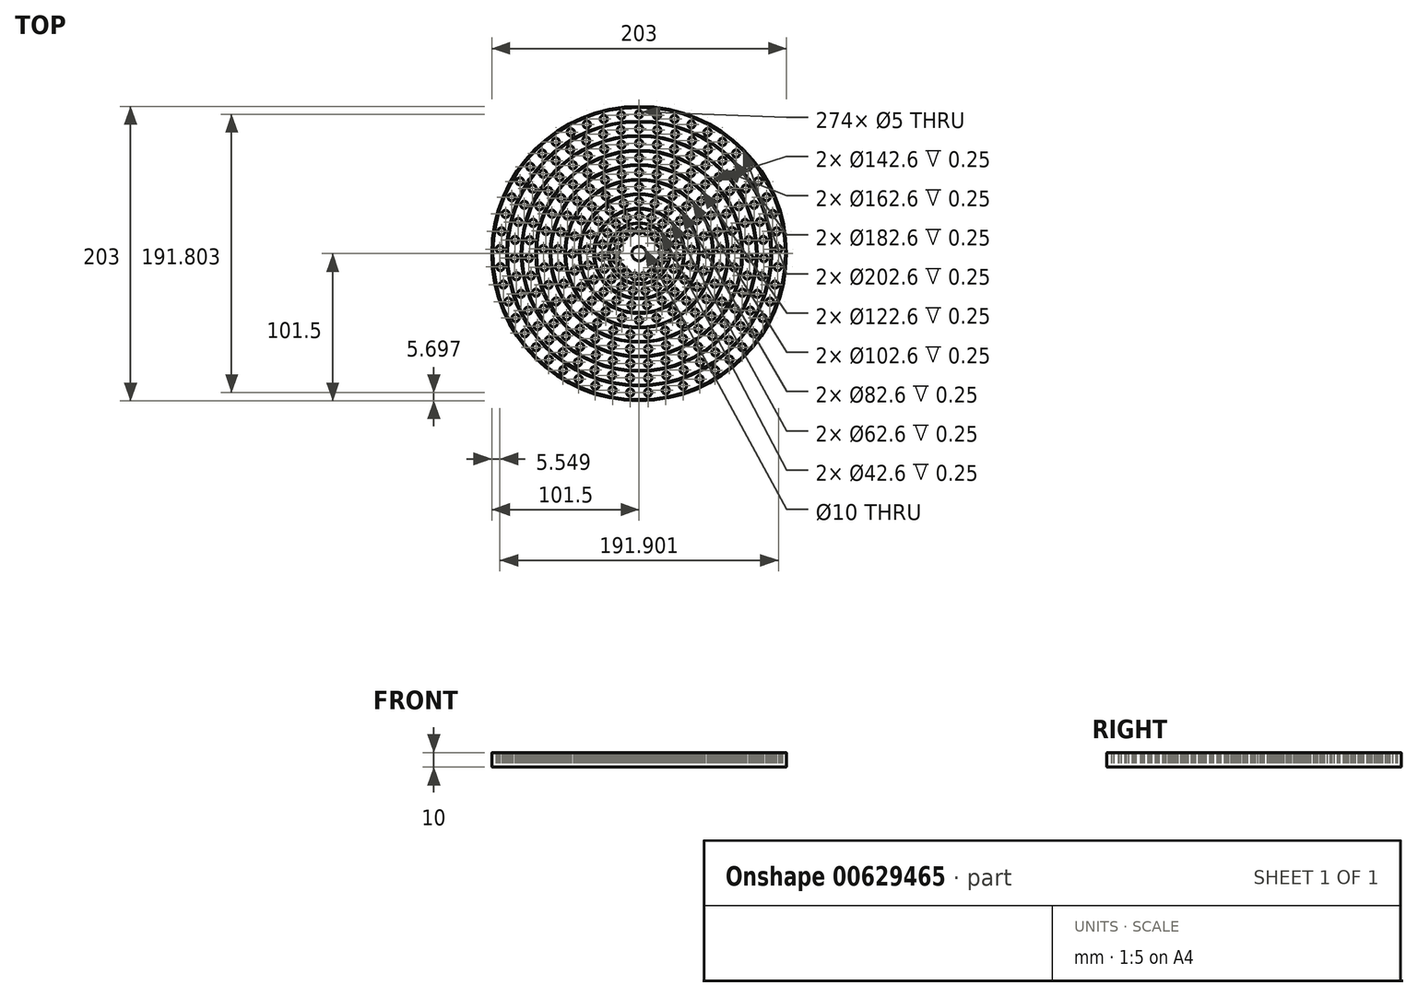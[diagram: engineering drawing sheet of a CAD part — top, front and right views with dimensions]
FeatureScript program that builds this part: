
annotation { "Feature Type Name" : "Feature", "Feature Type Description" : "" }
export const myFeature = defineFeature(function(context is Context, id is Id, definition is map)
    precondition{}
    {
        {
            var Q0;
            Q0=qCreatedBy(makeId("Top.planeOp"),FACE);
            var sketch = newSketch(context, id + "F0", { "sketchPlane" : qUnion([Q0])});
            skCircle(sketch, "E0", {"center": v(0, 0) * mm, "radius": 101.5 * mm});
            skCircle(sketch, "E1", {"center": v(0, 16) * mm, "radius": 2.5 * mm});
            skCircle(sketch, "E2.0.1.0", {"center": v(0, 26) * mm, "radius": 2.5 * mm});
            skCircle(sketch, "E2.0.2.0", {"center": v(0, 36) * mm, "radius": 2.5 * mm});
            skCircle(sketch, "E2.0.3.0", {"center": v(0, 46) * mm, "radius": 2.5 * mm});
            skCircle(sketch, "E2.0.4.0", {"center": v(0, 56) * mm, "radius": 2.5 * mm});
            skCircle(sketch, "E2.0.5.0", {"center": v(0, 66) * mm, "radius": 2.5 * mm});
            skCircle(sketch, "E2.0.6.0", {"center": v(0, 76) * mm, "radius": 2.5 * mm});
            skCircle(sketch, "E2.0.7.0", {"center": v(0, 86) * mm, "radius": 2.5 * mm});
            skCircle(sketch, "E2.0.8.0", {"center": v(0, 96) * mm, "radius": 2.5 * mm});
            skLineSegment(sketch, "E2.direction1", {"start": v(0, 16) * mm, "end": v(25, 16) * mm, "construction": true});
            skLineSegment(sketch, "E2.direction2", {"start": v(0, 16) * mm, "end": v(0, 26) * mm, "construction": true});
            skCircle(sketch, "E3.1.0", {"center": v(-5.78, 14.92) * mm, "radius": 2.5 * mm});
            skCircle(sketch, "E3.2.0", {"center": v(-10.78, 11.82) * mm, "radius": 2.5 * mm});
            skCircle(sketch, "E4.1.3.0", {"center": v(-14.32, 7.13) * mm, "radius": 2.5 * mm});
            skCircle(sketch, "E5.1.0", {"center": v(-8.44, 24.6) * mm, "radius": 2.5 * mm});
            skCircle(sketch, "E5.2.0", {"center": v(-15.97, 20.52) * mm, "radius": 2.5 * mm});
            skCircle(sketch, "E5.3.0", {"center": v(-21.77, 14.22) * mm, "radius": 2.5 * mm});
            skCircle(sketch, "E5.4.0", {"center": v(-25.2, 6.38) * mm, "radius": 2.5 * mm});
            skCircle(sketch, "E5.5.0", {"center": v(-25.91, -2.15) * mm, "radius": 2.5 * mm});
            skCircle(sketch, "E6.1.0", {"center": v(-10.61, 34.4) * mm, "radius": 2.5 * mm});
            skCircle(sketch, "E6.2.0", {"center": v(-20.28, 29.74) * mm, "radius": 2.5 * mm});
            skCircle(sketch, "E6.3.0", {"center": v(-28.15, 22.45) * mm, "radius": 2.5 * mm});
            skCircle(sketch, "E6.4.0", {"center": v(-33.51, 13.15) * mm, "radius": 2.5 * mm});
            skCircle(sketch, "E6.5.0", {"center": v(-35.9, 2.7) * mm, "radius": 2.5 * mm});
            skCircle(sketch, "E6.6.0", {"center": v(-35.1, -8.01) * mm, "radius": 2.5 * mm});
            skCircle(sketch, "E6.7.0", {"center": v(-31.18, -18) * mm, "radius": 2.5 * mm});
            skCircle(sketch, "E7.1.0", {"center": v(-11.9, 44.43) * mm, "radius": 2.5 * mm});
            skCircle(sketch, "E7.2.0", {"center": v(-23, 39.84) * mm, "radius": 2.5 * mm});
            skCircle(sketch, "E7.3.0", {"center": v(-32.53, 32.53) * mm, "radius": 2.5 * mm});
            skCircle(sketch, "E7.4.0", {"center": v(-39.84, 23) * mm, "radius": 2.5 * mm});
            skCircle(sketch, "E7.5.0", {"center": v(-44.43, 11.9) * mm, "radius": 2.5 * mm});
            skCircle(sketch, "E7.6.0", {"center": v(-46, 0) * mm, "radius": 2.5 * mm});
            skCircle(sketch, "E7.7.0", {"center": v(-44.43, -11.9) * mm, "radius": 2.5 * mm});
            skCircle(sketch, "E7.8.0", {"center": v(-39.84, -23) * mm, "radius": 2.5 * mm});
            skCircle(sketch, "E7.9.0", {"center": v(-32.53, -32.53) * mm, "radius": 2.5 * mm});
            skCircle(sketch, "E8.1.0", {"center": v(-12.5, 64.8) * mm, "radius": 2.5 * mm});
            skCircle(sketch, "E8.2.0", {"center": v(-24.53, 61.27) * mm, "radius": 2.5 * mm});
            skCircle(sketch, "E8.3.0", {"center": v(-35.68, 55.52) * mm, "radius": 2.5 * mm});
            skCircle(sketch, "E8.4.0", {"center": v(-45.55, 47.77) * mm, "radius": 2.5 * mm});
            skCircle(sketch, "E8.5.0", {"center": v(-53.76, 38.28) * mm, "radius": 2.5 * mm});
            skCircle(sketch, "E8.6.0", {"center": v(-60.04, 27.42) * mm, "radius": 2.5 * mm});
            skCircle(sketch, "E8.7.0", {"center": v(-64.14, 15.56) * mm, "radius": 2.5 * mm});
            skCircle(sketch, "E8.8.0", {"center": v(-65.93, 3.14) * mm, "radius": 2.5 * mm});
            skCircle(sketch, "E8.9.0", {"center": v(-65.33, -9.4) * mm, "radius": 2.5 * mm});
            skCircle(sketch, "E8.10.0", {"center": v(-62.37, -21.59) * mm, "radius": 2.5 * mm});
            skCircle(sketch, "E8.11.0", {"center": v(-57.16, -33) * mm, "radius": 2.5 * mm});
            skCircle(sketch, "E9.1.0", {"center": v(-12.2, 75.02) * mm, "radius": 2.5 * mm});
            skCircle(sketch, "E9.2.0", {"center": v(-24.07, 72.09) * mm, "radius": 2.5 * mm});
            skCircle(sketch, "E9.3.0", {"center": v(-35.32, 67.3) * mm, "radius": 2.5 * mm});
            skCircle(sketch, "E9.4.0", {"center": v(-45.66, 60.76) * mm, "radius": 2.5 * mm});
            skCircle(sketch, "E9.5.0", {"center": v(-54.81, 52.65) * mm, "radius": 2.5 * mm});
            skCircle(sketch, "E9.6.0", {"center": v(-62.55, 43.17) * mm, "radius": 2.5 * mm});
            skCircle(sketch, "E9.7.0", {"center": v(-68.66, 32.58) * mm, "radius": 2.5 * mm});
            skCircle(sketch, "E9.8.0", {"center": v(-73, 21.14) * mm, "radius": 2.5 * mm});
            skCircle(sketch, "E9.9.0", {"center": v(-75.45, 9.16) * mm, "radius": 2.5 * mm});
            skCircle(sketch, "E9.10.0", {"center": v(-75.94, -3.06) * mm, "radius": 2.5 * mm});
            skCircle(sketch, "E9.11.0", {"center": v(-74.46, -15.2) * mm, "radius": 2.5 * mm});
            skCircle(sketch, "E9.12.0", {"center": v(-71.06, -26.95) * mm, "radius": 2.5 * mm});
            skCircle(sketch, "E9.13.0", {"center": v(-65.82, -38) * mm, "radius": 2.5 * mm});
            skCircle(sketch, "E9.14.0", {"center": v(-58.87, -48.07) * mm, "radius": 2.5 * mm});
            skCircle(sketch, "E9.15.0", {"center": v(-50.4, -56.89) * mm, "radius": 2.5 * mm});
            skCircle(sketch, "E10.1.0", {"center": v(-12.28, 95.21) * mm, "radius": 2.5 * mm});
            skCircle(sketch, "E10.2.0", {"center": v(-24.35, 92.86) * mm, "radius": 2.5 * mm});
            skCircle(sketch, "E10.3.0", {"center": v(-36.03, 88.98) * mm, "radius": 2.5 * mm});
            skCircle(sketch, "E10.4.0", {"center": v(-47.1, 83.65) * mm, "radius": 2.5 * mm});
            skCircle(sketch, "E10.5.0", {"center": v(-57.42, 76.94) * mm, "radius": 2.5 * mm});
            skCircle(sketch, "E10.6.0", {"center": v(-66.79, 68.96) * mm, "radius": 2.5 * mm});
            skCircle(sketch, "E10.7.0", {"center": v(-75.06, 59.86) * mm, "radius": 2.5 * mm});
            skCircle(sketch, "E10.8.0", {"center": v(-82.1, 49.77) * mm, "radius": 2.5 * mm});
            skCircle(sketch, "E10.9.0", {"center": v(-87.78, 38.86) * mm, "radius": 2.5 * mm});
            skCircle(sketch, "E10.10.0", {"center": v(-92.03, 27.31) * mm, "radius": 2.5 * mm});
            skCircle(sketch, "E10.11.0", {"center": v(-94.77, 15.32) * mm, "radius": 2.5 * mm});
            skCircle(sketch, "E10.12.0", {"center": v(-95.95, 3.08) * mm, "radius": 2.5 * mm});
            skCircle(sketch, "E10.13.0", {"center": v(-95.56, -9.22) * mm, "radius": 2.5 * mm});
            skCircle(sketch, "E10.14.0", {"center": v(-93.6, -21.36) * mm, "radius": 2.5 * mm});
            skCircle(sketch, "E10.15.0", {"center": v(-90.1, -33.16) * mm, "radius": 2.5 * mm});
            skCircle(sketch, "E10.16.0", {"center": v(-85.11, -44.4) * mm, "radius": 2.5 * mm});
            skCircle(sketch, "E10.17.0", {"center": v(-78.74, -54.92) * mm, "radius": 2.5 * mm});
            skCircle(sketch, "E11.1.4.0", {"center": v(-15.93, 1.48) * mm, "radius": 2.5 * mm});
            skCircle(sketch, "E11.1.5.0", {"center": v(-15.39, -4.38) * mm, "radius": 2.5 * mm});
            skCircle(sketch, "E11.1.6.0", {"center": v(-12.77, -9.64) * mm, "radius": 2.5 * mm});
            skCircle(sketch, "E11.1.7.0", {"center": v(-8.42, -13.6) * mm, "radius": 2.5 * mm});
            skCircle(sketch, "E11.1.8.0", {"center": v(-2.94, -15.73) * mm, "radius": 2.5 * mm});
            skCircle(sketch, "E11.1.9.0", {"center": v(2.94, -15.73) * mm, "radius": 2.5 * mm});
            skCircle(sketch, "E11.1.10.0", {"center": v(8.42, -13.6) * mm, "radius": 2.5 * mm});
            skCircle(sketch, "E11.1.11.0", {"center": v(12.77, -9.64) * mm, "radius": 2.5 * mm});
            skCircle(sketch, "E11.1.12.0", {"center": v(15.39, -4.38) * mm, "radius": 2.5 * mm});
            skCircle(sketch, "E11.1.13.0", {"center": v(15.93, 1.48) * mm, "radius": 2.5 * mm});
            skCircle(sketch, "E11.1.14.0", {"center": v(14.32, 7.13) * mm, "radius": 2.5 * mm});
            skCircle(sketch, "E11.1.15.0", {"center": v(10.78, 11.82) * mm, "radius": 2.5 * mm});
            skCircle(sketch, "E11.1.16.0", {"center": v(5.78, 14.92) * mm, "radius": 2.5 * mm});
            skCircle(sketch, "E12.1.6.0", {"center": v(-23.81, -10.44) * mm, "radius": 2.5 * mm});
            skCircle(sketch, "E12.1.7.0", {"center": v(-19.13, -17.6) * mm, "radius": 2.5 * mm});
            skCircle(sketch, "E12.1.8.0", {"center": v(-12.37, -22.87) * mm, "radius": 2.5 * mm});
            skCircle(sketch, "E12.1.9.0", {"center": v(-4.28, -25.65) * mm, "radius": 2.5 * mm});
            skCircle(sketch, "E12.1.10.0", {"center": v(4.28, -25.65) * mm, "radius": 2.5 * mm});
            skCircle(sketch, "E12.1.11.0", {"center": v(12.37, -22.87) * mm, "radius": 2.5 * mm});
            skCircle(sketch, "E12.1.12.0", {"center": v(19.13, -17.6) * mm, "radius": 2.5 * mm});
            skCircle(sketch, "E12.1.13.0", {"center": v(23.81, -10.44) * mm, "radius": 2.5 * mm});
            skCircle(sketch, "E12.1.14.0", {"center": v(25.91, -2.15) * mm, "radius": 2.5 * mm});
            skCircle(sketch, "E12.1.15.0", {"center": v(25.2, 6.38) * mm, "radius": 2.5 * mm});
            skCircle(sketch, "E12.1.16.0", {"center": v(21.77, 14.22) * mm, "radius": 2.5 * mm});
            skCircle(sketch, "E12.1.17.0", {"center": v(15.97, 20.52) * mm, "radius": 2.5 * mm});
            skCircle(sketch, "E12.1.18.0", {"center": v(8.44, 24.6) * mm, "radius": 2.5 * mm});
            skCircle(sketch, "E13.1.8.0", {"center": v(-24.49, -26.39) * mm, "radius": 2.5 * mm});
            skCircle(sketch, "E13.1.9.0", {"center": v(-15.62, -32.43) * mm, "radius": 2.5 * mm});
            skCircle(sketch, "E13.1.10.0", {"center": v(-5.37, -35.6) * mm, "radius": 2.5 * mm});
            skCircle(sketch, "E13.1.11.0", {"center": v(5.37, -35.6) * mm, "radius": 2.5 * mm});
            skCircle(sketch, "E13.1.12.0", {"center": v(15.62, -32.43) * mm, "radius": 2.5 * mm});
            skCircle(sketch, "E13.1.13.0", {"center": v(24.49, -26.39) * mm, "radius": 2.5 * mm});
            skCircle(sketch, "E13.1.14.0", {"center": v(31.18, -18) * mm, "radius": 2.5 * mm});
            skCircle(sketch, "E13.1.15.0", {"center": v(35.1, -8.01) * mm, "radius": 2.5 * mm});
            skCircle(sketch, "E13.1.16.0", {"center": v(35.9, 2.7) * mm, "radius": 2.5 * mm});
            skCircle(sketch, "E13.1.17.0", {"center": v(33.51, 13.15) * mm, "radius": 2.5 * mm});
            skCircle(sketch, "E13.1.18.0", {"center": v(28.15, 22.45) * mm, "radius": 2.5 * mm});
            skCircle(sketch, "E13.1.19.0", {"center": v(20.28, 29.74) * mm, "radius": 2.5 * mm});
            skCircle(sketch, "E13.1.20.0", {"center": v(10.61, 34.4) * mm, "radius": 2.5 * mm});
            skCircle(sketch, "E14.1.10.0", {"center": v(-23, -39.84) * mm, "radius": 2.5 * mm});
            skCircle(sketch, "E14.1.11.0", {"center": v(-11.9, -44.43) * mm, "radius": 2.5 * mm});
            skCircle(sketch, "E14.1.12.0", {"center": v(0, -46) * mm, "radius": 2.5 * mm});
            skCircle(sketch, "E14.1.13.0", {"center": v(11.9, -44.43) * mm, "radius": 2.5 * mm});
            skCircle(sketch, "E14.1.14.0", {"center": v(23, -39.84) * mm, "radius": 2.5 * mm});
            skCircle(sketch, "E14.1.15.0", {"center": v(32.53, -32.53) * mm, "radius": 2.5 * mm});
            skCircle(sketch, "E14.1.16.0", {"center": v(39.84, -23) * mm, "radius": 2.5 * mm});
            skCircle(sketch, "E14.1.17.0", {"center": v(44.43, -11.9) * mm, "radius": 2.5 * mm});
            skCircle(sketch, "E14.1.18.0", {"center": v(46, 0) * mm, "radius": 2.5 * mm});
            skCircle(sketch, "E14.1.19.0", {"center": v(44.43, 11.9) * mm, "radius": 2.5 * mm});
            skCircle(sketch, "E14.1.20.0", {"center": v(39.84, 23) * mm, "radius": 2.5 * mm});
            skCircle(sketch, "E14.1.21.0", {"center": v(32.53, 32.53) * mm, "radius": 2.5 * mm});
            skCircle(sketch, "E14.1.22.0", {"center": v(23, 39.84) * mm, "radius": 2.5 * mm});
            skCircle(sketch, "E14.1.23.0", {"center": v(11.9, 44.43) * mm, "radius": 2.5 * mm});
            skCircle(sketch, "E15.1.0", {"center": v(-12.04, 54.7) * mm, "radius": 2.5 * mm});
            skCircle(sketch, "E15.2.0", {"center": v(-23.51, 50.82) * mm, "radius": 2.5 * mm});
            skCircle(sketch, "E16.1.3.0", {"center": v(-33.89, 44.58) * mm, "radius": 2.5 * mm});
            skCircle(sketch, "E16.1.4.0", {"center": v(-42.68, 36.25) * mm, "radius": 2.5 * mm});
            skCircle(sketch, "E16.1.5.0", {"center": v(-49.48, 26.23) * mm, "radius": 2.5 * mm});
            skCircle(sketch, "E16.1.6.0", {"center": v(-53.96, 14.98) * mm, "radius": 2.5 * mm});
            skCircle(sketch, "E16.1.7.0", {"center": v(-55.92, 3.03) * mm, "radius": 2.5 * mm});
            skCircle(sketch, "E16.1.8.0", {"center": v(-55.26, -9.06) * mm, "radius": 2.5 * mm});
            skCircle(sketch, "E16.1.9.0", {"center": v(-52.02, -20.73) * mm, "radius": 2.5 * mm});
            skCircle(sketch, "E16.1.10.0", {"center": v(-46.35, -31.43) * mm, "radius": 2.5 * mm});
            skCircle(sketch, "E16.1.11.0", {"center": v(-38.51, -40.66) * mm, "radius": 2.5 * mm});
            skCircle(sketch, "E16.1.12.0", {"center": v(-28.87, -47.98) * mm, "radius": 2.5 * mm});
            skCircle(sketch, "E16.1.13.0", {"center": v(-17.88, -53.07) * mm, "radius": 2.5 * mm});
            skCircle(sketch, "E16.1.14.0", {"center": v(-6.05, -55.67) * mm, "radius": 2.5 * mm});
            skCircle(sketch, "E16.1.15.0", {"center": v(6.05, -55.67) * mm, "radius": 2.5 * mm});
            skCircle(sketch, "E16.1.16.0", {"center": v(17.88, -53.07) * mm, "radius": 2.5 * mm});
            skCircle(sketch, "E16.1.17.0", {"center": v(28.87, -47.98) * mm, "radius": 2.5 * mm});
            skCircle(sketch, "E16.1.18.0", {"center": v(38.51, -40.66) * mm, "radius": 2.5 * mm});
            skCircle(sketch, "E16.1.19.0", {"center": v(46.35, -31.43) * mm, "radius": 2.5 * mm});
            skCircle(sketch, "E16.1.20.0", {"center": v(52.02, -20.73) * mm, "radius": 2.5 * mm});
            skCircle(sketch, "E16.1.21.0", {"center": v(55.26, -9.06) * mm, "radius": 2.5 * mm});
            skCircle(sketch, "E16.1.22.0", {"center": v(55.92, 3.03) * mm, "radius": 2.5 * mm});
            skCircle(sketch, "E16.1.23.0", {"center": v(53.96, 14.98) * mm, "radius": 2.5 * mm});
            skCircle(sketch, "E16.1.24.0", {"center": v(49.48, 26.23) * mm, "radius": 2.5 * mm});
            skCircle(sketch, "E16.1.25.0", {"center": v(42.68, 36.25) * mm, "radius": 2.5 * mm});
            skCircle(sketch, "E16.1.26.0", {"center": v(33.89, 44.58) * mm, "radius": 2.5 * mm});
            skCircle(sketch, "E16.1.27.0", {"center": v(23.51, 50.82) * mm, "radius": 2.5 * mm});
            skCircle(sketch, "E16.1.28.0", {"center": v(12.04, 54.7) * mm, "radius": 2.5 * mm});
            skCircle(sketch, "E17.1.12.0", {"center": v(-49.88, -43.22) * mm, "radius": 2.5 * mm});
            skCircle(sketch, "E17.1.13.0", {"center": v(-40.8, -51.88) * mm, "radius": 2.5 * mm});
            skCircle(sketch, "E17.1.14.0", {"center": v(-30.24, -58.66) * mm, "radius": 2.5 * mm});
            skCircle(sketch, "E17.1.15.0", {"center": v(-18.6, -63.33) * mm, "radius": 2.5 * mm});
            skCircle(sketch, "E17.1.16.0", {"center": v(-6.27, -65.7) * mm, "radius": 2.5 * mm});
            skCircle(sketch, "E17.1.17.0", {"center": v(6.27, -65.7) * mm, "radius": 2.5 * mm});
            skCircle(sketch, "E17.1.18.0", {"center": v(18.6, -63.33) * mm, "radius": 2.5 * mm});
            skCircle(sketch, "E17.1.19.0", {"center": v(30.24, -58.66) * mm, "radius": 2.5 * mm});
            skCircle(sketch, "E17.1.20.0", {"center": v(40.8, -51.88) * mm, "radius": 2.5 * mm});
            skCircle(sketch, "E17.1.21.0", {"center": v(49.88, -43.22) * mm, "radius": 2.5 * mm});
            skCircle(sketch, "E17.1.22.0", {"center": v(57.16, -33) * mm, "radius": 2.5 * mm});
            skCircle(sketch, "E17.1.23.0", {"center": v(62.37, -21.59) * mm, "radius": 2.5 * mm});
            skCircle(sketch, "E17.1.24.0", {"center": v(65.33, -9.4) * mm, "radius": 2.5 * mm});
            skCircle(sketch, "E17.1.25.0", {"center": v(65.93, 3.14) * mm, "radius": 2.5 * mm});
            skCircle(sketch, "E17.1.26.0", {"center": v(64.14, 15.56) * mm, "radius": 2.5 * mm});
            skCircle(sketch, "E17.1.27.0", {"center": v(60.04, 27.42) * mm, "radius": 2.5 * mm});
            skCircle(sketch, "E17.1.28.0", {"center": v(53.76, 38.28) * mm, "radius": 2.5 * mm});
            skCircle(sketch, "E18.1.29.0", {"center": v(45.55, 47.77) * mm, "radius": 2.5 * mm});
            skCircle(sketch, "E18.1.30.0", {"center": v(35.68, 55.52) * mm, "radius": 2.5 * mm});
            skCircle(sketch, "E18.1.31.0", {"center": v(24.53, 61.27) * mm, "radius": 2.5 * mm});
            skCircle(sketch, "E18.1.32.0", {"center": v(12.5, 64.8) * mm, "radius": 2.5 * mm});
            skCircle(sketch, "E19.1.16.0", {"center": v(-40.62, -64.23) * mm, "radius": 2.5 * mm});
            skCircle(sketch, "E19.1.17.0", {"center": v(-29.79, -69.92) * mm, "radius": 2.5 * mm});
            skCircle(sketch, "E19.1.18.0", {"center": v(-18.19, -73.8) * mm, "radius": 2.5 * mm});
            skCircle(sketch, "E19.1.19.0", {"center": v(-6.12, -75.75) * mm, "radius": 2.5 * mm});
            skCircle(sketch, "E19.1.20.0", {"center": v(6.12, -75.75) * mm, "radius": 2.5 * mm});
            skCircle(sketch, "E19.1.21.0", {"center": v(18.19, -73.8) * mm, "radius": 2.5 * mm});
            skCircle(sketch, "E19.1.22.0", {"center": v(29.79, -69.92) * mm, "radius": 2.5 * mm});
            skCircle(sketch, "E19.1.23.0", {"center": v(40.62, -64.23) * mm, "radius": 2.5 * mm});
            skCircle(sketch, "E19.1.24.0", {"center": v(50.4, -56.89) * mm, "radius": 2.5 * mm});
            skCircle(sketch, "E19.1.25.0", {"center": v(58.87, -48.07) * mm, "radius": 2.5 * mm});
            skCircle(sketch, "E19.1.26.0", {"center": v(65.82, -38) * mm, "radius": 2.5 * mm});
            skCircle(sketch, "E19.1.27.0", {"center": v(71.06, -26.95) * mm, "radius": 2.5 * mm});
            skCircle(sketch, "E19.1.28.0", {"center": v(74.46, -15.2) * mm, "radius": 2.5 * mm});
            skCircle(sketch, "E19.1.29.0", {"center": v(75.94, -3.06) * mm, "radius": 2.5 * mm});
            skCircle(sketch, "E19.1.30.0", {"center": v(75.45, 9.16) * mm, "radius": 2.5 * mm});
            skCircle(sketch, "E19.1.31.0", {"center": v(73, 21.14) * mm, "radius": 2.5 * mm});
            skCircle(sketch, "E19.1.32.0", {"center": v(68.66, 32.58) * mm, "radius": 2.5 * mm});
            skCircle(sketch, "E19.1.33.0", {"center": v(62.55, 43.17) * mm, "radius": 2.5 * mm});
            skCircle(sketch, "E19.1.34.0", {"center": v(54.81, 52.65) * mm, "radius": 2.5 * mm});
            skCircle(sketch, "E19.1.35.0", {"center": v(45.66, 60.76) * mm, "radius": 2.5 * mm});
            skCircle(sketch, "E19.1.36.0", {"center": v(35.32, 67.3) * mm, "radius": 2.5 * mm});
            skCircle(sketch, "E19.1.37.0", {"center": v(24.07, 72.09) * mm, "radius": 2.5 * mm});
            skCircle(sketch, "E19.1.38.0", {"center": v(12.2, 75.02) * mm, "radius": 2.5 * mm});
            skCircle(sketch, "E20.1.18.0", {"center": v(-71.07, -64.54) * mm, "radius": 2.5 * mm});
            skCircle(sketch, "E20.1.19.0", {"center": v(-62.23, -73.1) * mm, "radius": 2.5 * mm});
            skCircle(sketch, "E20.1.20.0", {"center": v(-52.37, -80.46) * mm, "radius": 2.5 * mm});
            skCircle(sketch, "E20.1.21.0", {"center": v(-41.65, -86.5) * mm, "radius": 2.5 * mm});
            skCircle(sketch, "E20.1.22.0", {"center": v(-30.25, -91.1) * mm, "radius": 2.5 * mm});
            skCircle(sketch, "E20.1.23.0", {"center": v(-18.35, -94.23) * mm, "radius": 2.5 * mm});
            skCircle(sketch, "E20.1.24.0", {"center": v(-6.15, -95.8) * mm, "radius": 2.5 * mm});
            skCircle(sketch, "E20.1.25.0", {"center": v(6.15, -95.8) * mm, "radius": 2.5 * mm});
            skCircle(sketch, "E20.1.26.0", {"center": v(18.35, -94.23) * mm, "radius": 2.5 * mm});
            skCircle(sketch, "E20.1.27.0", {"center": v(30.25, -91.1) * mm, "radius": 2.5 * mm});
            skCircle(sketch, "E20.1.28.0", {"center": v(41.65, -86.5) * mm, "radius": 2.5 * mm});
            skCircle(sketch, "E20.1.29.0", {"center": v(52.37, -80.46) * mm, "radius": 2.5 * mm});
            skCircle(sketch, "E20.1.30.0", {"center": v(62.23, -73.1) * mm, "radius": 2.5 * mm});
            skCircle(sketch, "E20.1.31.0", {"center": v(71.07, -64.54) * mm, "radius": 2.5 * mm});
            skCircle(sketch, "E20.1.32.0", {"center": v(78.74, -54.92) * mm, "radius": 2.5 * mm});
            skCircle(sketch, "E20.1.33.0", {"center": v(85.11, -44.4) * mm, "radius": 2.5 * mm});
            skCircle(sketch, "E20.1.34.0", {"center": v(90.1, -33.16) * mm, "radius": 2.5 * mm});
            skCircle(sketch, "E20.1.35.0", {"center": v(93.6, -21.36) * mm, "radius": 2.5 * mm});
            skCircle(sketch, "E20.1.36.0", {"center": v(95.56, -9.22) * mm, "radius": 2.5 * mm});
            skCircle(sketch, "E20.1.37.0", {"center": v(95.95, 3.08) * mm, "radius": 2.5 * mm});
            skCircle(sketch, "E20.1.38.0", {"center": v(94.77, 15.32) * mm, "radius": 2.5 * mm});
            skCircle(sketch, "E20.1.39.0", {"center": v(92.03, 27.31) * mm, "radius": 2.5 * mm});
            skCircle(sketch, "E20.1.40.0", {"center": v(87.78, 38.86) * mm, "radius": 2.5 * mm});
            skCircle(sketch, "E20.1.41.0", {"center": v(82.1, 49.77) * mm, "radius": 2.5 * mm});
            skCircle(sketch, "E20.1.42.0", {"center": v(75.06, 59.86) * mm, "radius": 2.5 * mm});
            skCircle(sketch, "E21.1.0", {"center": v(-12.52, 85.08) * mm, "radius": 2.5 * mm});
            skCircle(sketch, "E21.2.0", {"center": v(-24.78, 82.35) * mm, "radius": 2.5 * mm});
            skCircle(sketch, "E22.1.3.0", {"center": v(-36.5, 77.87) * mm, "radius": 2.5 * mm});
            skCircle(sketch, "E22.1.4.0", {"center": v(-47.45, 71.72) * mm, "radius": 2.5 * mm});
            skCircle(sketch, "E22.1.5.0", {"center": v(-57.39, 64.05) * mm, "radius": 2.5 * mm});
            skCircle(sketch, "E22.1.6.0", {"center": v(-66.1, 55.01) * mm, "radius": 2.5 * mm});
            skCircle(sketch, "E22.1.7.0", {"center": v(-73.4, 44.8) * mm, "radius": 2.5 * mm});
            skCircle(sketch, "E22.1.8.0", {"center": v(-79.15, 33.64) * mm, "radius": 2.5 * mm});
            skCircle(sketch, "E22.1.9.0", {"center": v(-83.2, 21.75) * mm, "radius": 2.5 * mm});
            skCircle(sketch, "E22.1.10.0", {"center": v(-85.48, 9.4) * mm, "radius": 2.5 * mm});
            skCircle(sketch, "E22.1.11.0", {"center": v(-85.94, -3.14) * mm, "radius": 2.5 * mm});
            skCircle(sketch, "E22.1.12.0", {"center": v(-84.57, -15.62) * mm, "radius": 2.5 * mm});
            skCircle(sketch, "E22.1.13.0", {"center": v(-81.4, -27.77) * mm, "radius": 2.5 * mm});
            skCircle(sketch, "E22.1.14.0", {"center": v(-76.48, -39.32) * mm, "radius": 2.5 * mm});
            skCircle(sketch, "E22.1.15.0", {"center": v(-69.94, -50.04) * mm, "radius": 2.5 * mm});
            skCircle(sketch, "E22.1.16.0", {"center": v(-61.91, -59.7) * mm, "radius": 2.5 * mm});
            skCircle(sketch, "E22.1.17.0", {"center": v(-52.56, -68.07) * mm, "radius": 2.5 * mm});
            skCircle(sketch, "E22.1.18.0", {"center": v(-42.09, -75) * mm, "radius": 2.5 * mm});
            skCircle(sketch, "E22.1.19.0", {"center": v(-30.72, -80.33) * mm, "radius": 2.5 * mm});
            skCircle(sketch, "E22.1.20.0", {"center": v(-18.7, -83.94) * mm, "radius": 2.5 * mm});
            skCircle(sketch, "E22.1.21.0", {"center": v(-6.28, -85.77) * mm, "radius": 2.5 * mm});
            skCircle(sketch, "E22.1.22.0", {"center": v(6.28, -85.77) * mm, "radius": 2.5 * mm});
            skCircle(sketch, "E22.1.23.0", {"center": v(18.7, -83.94) * mm, "radius": 2.5 * mm});
            skCircle(sketch, "E22.1.24.0", {"center": v(30.72, -80.33) * mm, "radius": 2.5 * mm});
            skCircle(sketch, "E22.1.25.0", {"center": v(42.09, -75) * mm, "radius": 2.5 * mm});
            skCircle(sketch, "E22.1.26.0", {"center": v(52.56, -68.07) * mm, "radius": 2.5 * mm});
            skCircle(sketch, "E22.1.27.0", {"center": v(61.91, -59.7) * mm, "radius": 2.5 * mm});
            skCircle(sketch, "E22.1.28.0", {"center": v(69.94, -50.04) * mm, "radius": 2.5 * mm});
            skCircle(sketch, "E22.1.29.0", {"center": v(76.48, -39.32) * mm, "radius": 2.5 * mm});
            skCircle(sketch, "E22.1.30.0", {"center": v(81.4, -27.77) * mm, "radius": 2.5 * mm});
            skCircle(sketch, "E22.1.31.0", {"center": v(84.57, -15.62) * mm, "radius": 2.5 * mm});
            skCircle(sketch, "E22.1.32.0", {"center": v(85.94, -3.14) * mm, "radius": 2.5 * mm});
            skCircle(sketch, "E22.1.33.0", {"center": v(85.48, 9.4) * mm, "radius": 2.5 * mm});
            skCircle(sketch, "E22.1.34.0", {"center": v(83.2, 21.75) * mm, "radius": 2.5 * mm});
            skCircle(sketch, "E22.1.35.0", {"center": v(79.15, 33.64) * mm, "radius": 2.5 * mm});
            skCircle(sketch, "E22.1.36.0", {"center": v(73.4, 44.8) * mm, "radius": 2.5 * mm});
            skCircle(sketch, "E22.1.37.0", {"center": v(66.1, 55.01) * mm, "radius": 2.5 * mm});
            skCircle(sketch, "E22.1.38.0", {"center": v(57.39, 64.05) * mm, "radius": 2.5 * mm});
            skCircle(sketch, "E22.1.39.0", {"center": v(47.45, 71.72) * mm, "radius": 2.5 * mm});
            skCircle(sketch, "E22.1.40.0", {"center": v(36.5, 77.87) * mm, "radius": 2.5 * mm});
            skCircle(sketch, "E22.1.41.0", {"center": v(24.78, 82.35) * mm, "radius": 2.5 * mm});
            skCircle(sketch, "E22.1.42.0", {"center": v(12.52, 85.08) * mm, "radius": 2.5 * mm});
            skCircle(sketch, "E23.1.43.0", {"center": v(66.79, 68.96) * mm, "radius": 2.5 * mm});
            skCircle(sketch, "E23.1.44.0", {"center": v(57.42, 76.94) * mm, "radius": 2.5 * mm});
            skCircle(sketch, "E23.1.45.0", {"center": v(47.1, 83.65) * mm, "radius": 2.5 * mm});
            skCircle(sketch, "E23.1.46.0", {"center": v(36.03, 88.98) * mm, "radius": 2.5 * mm});
            skCircle(sketch, "E23.1.47.0", {"center": v(24.35, 92.86) * mm, "radius": 2.5 * mm});
            skCircle(sketch, "E23.1.48.0", {"center": v(12.28, 95.21) * mm, "radius": 2.5 * mm});
            skCircle(sketch, "E24", {"center": v(0, 0) * mm, "radius": 5 * mm});
            skLineSegment(sketch, "E25.bottom", {"start": v(1.7, -6.57) * mm, "end": v(-1.7, -6.57) * mm, "construction": true});
            skLineSegment(sketch, "E25.top", {"start": v(1.7, -3.43) * mm, "end": v(-1.7, -3.43) * mm});
            skLineSegment(sketch, "E25.left", {"start": v(1.7, -6.57) * mm, "end": v(1.7, -3.43) * mm});
            skLineSegment(sketch, "E25.right", {"start": v(-1.7, -6.57) * mm, "end": v(-1.7, -3.43) * mm});
            skPoint(sketch, "E25.middle", {"position": v(0, -5) * mm});
            skSolve(sketch);
        }
        {
            var Q0;
            Q0=makeQuery(id+"F0.imprint","IMPRINT",FACE,{"disambiguationData":[TD([[makeQuery(id+"F0.imprint","IMPRINT",EDGE,{"derivedFrom":sQuery(id+"F0.wireOp",EDGE,"E0")}),1.0]])]});
            extrude(context, id + "F1", {"entities" : qUnion([Q0]), "depth" : 10 * mm, "offsetDistance" : 25 * mm});
        }
        {
            var Q0;
            Q0=qCreatedBy(makeId("Right.planeOp"),FACE);
            var sketch = newSketch(context, id + "F2", { "sketchPlane" : qUnion([Q0])});
            skPoint(sketch, "E26", {"position": v(21, 0) * mm});
            skLineSegment(sketch, "E27.bottom", {"start": v(21.3, 0.25) * mm, "end": v(20.7, 0.25) * mm});
            skLineSegment(sketch, "E27.top", {"start": v(21.3, -0.25) * mm, "end": v(20.7, -0.25) * mm});
            skLineSegment(sketch, "E27.left", {"start": v(21.3, 0.25) * mm, "end": v(21.3, -0.25) * mm});
            skLineSegment(sketch, "E27.right", {"start": v(20.7, 0.25) * mm, "end": v(20.7, -0.25) * mm});
            skLineSegment(sketch, "E28.1.0.0", {"start": v(31.3, -0.25) * mm, "end": v(30.7, -0.25) * mm});
            skLineSegment(sketch, "E28.1.0.1", {"start": v(30.7, 0.25) * mm, "end": v(30.7, -0.25) * mm});
            skLineSegment(sketch, "E28.1.0.2", {"start": v(31.3, 0.25) * mm, "end": v(30.7, 0.25) * mm});
            skLineSegment(sketch, "E28.1.0.3", {"start": v(31.3, 0.25) * mm, "end": v(31.3, -0.25) * mm});
            skLineSegment(sketch, "E28.2.0.0", {"start": v(41.3, -0.25) * mm, "end": v(40.7, -0.25) * mm});
            skLineSegment(sketch, "E28.2.0.1", {"start": v(40.7, 0.25) * mm, "end": v(40.7, -0.25) * mm});
            skLineSegment(sketch, "E28.2.0.2", {"start": v(41.3, 0.25) * mm, "end": v(40.7, 0.25) * mm});
            skLineSegment(sketch, "E28.2.0.3", {"start": v(41.3, 0.25) * mm, "end": v(41.3, -0.25) * mm});
            skLineSegment(sketch, "E28.3.0.0", {"start": v(51.3, -0.25) * mm, "end": v(50.7, -0.25) * mm});
            skLineSegment(sketch, "E28.3.0.1", {"start": v(50.7, 0.25) * mm, "end": v(50.7, -0.25) * mm});
            skLineSegment(sketch, "E28.3.0.2", {"start": v(51.3, 0.25) * mm, "end": v(50.7, 0.25) * mm});
            skLineSegment(sketch, "E28.3.0.3", {"start": v(51.3, 0.25) * mm, "end": v(51.3, -0.25) * mm});
            skLineSegment(sketch, "E28.4.0.0", {"start": v(61.3, -0.25) * mm, "end": v(60.7, -0.25) * mm});
            skLineSegment(sketch, "E28.4.0.1", {"start": v(60.7, 0.25) * mm, "end": v(60.7, -0.25) * mm});
            skLineSegment(sketch, "E28.4.0.2", {"start": v(61.3, 0.25) * mm, "end": v(60.7, 0.25) * mm});
            skLineSegment(sketch, "E28.4.0.3", {"start": v(61.3, 0.25) * mm, "end": v(61.3, -0.25) * mm});
            skLineSegment(sketch, "E28.5.0.0", {"start": v(71.3, -0.25) * mm, "end": v(70.7, -0.25) * mm});
            skLineSegment(sketch, "E28.5.0.1", {"start": v(70.7, 0.25) * mm, "end": v(70.7, -0.25) * mm});
            skLineSegment(sketch, "E28.5.0.2", {"start": v(71.3, 0.25) * mm, "end": v(70.7, 0.25) * mm});
            skLineSegment(sketch, "E28.5.0.3", {"start": v(71.3, 0.25) * mm, "end": v(71.3, -0.25) * mm});
            skLineSegment(sketch, "E28.6.0.0", {"start": v(81.3, -0.25) * mm, "end": v(80.7, -0.25) * mm});
            skLineSegment(sketch, "E28.6.0.1", {"start": v(80.7, 0.25) * mm, "end": v(80.7, -0.25) * mm});
            skLineSegment(sketch, "E28.6.0.2", {"start": v(81.3, 0.25) * mm, "end": v(80.7, 0.25) * mm});
            skLineSegment(sketch, "E28.6.0.3", {"start": v(81.3, 0.25) * mm, "end": v(81.3, -0.25) * mm});
            skLineSegment(sketch, "E28.7.0.0", {"start": v(91.3, -0.25) * mm, "end": v(90.7, -0.25) * mm});
            skLineSegment(sketch, "E28.7.0.1", {"start": v(90.7, 0.25) * mm, "end": v(90.7, -0.25) * mm});
            skLineSegment(sketch, "E28.7.0.2", {"start": v(91.3, 0.25) * mm, "end": v(90.7, 0.25) * mm});
            skLineSegment(sketch, "E28.7.0.3", {"start": v(91.3, 0.25) * mm, "end": v(91.3, -0.25) * mm});
            skLineSegment(sketch, "E28.8.0.0", {"start": v(101.3, -0.25) * mm, "end": v(100.7, -0.25) * mm});
            skLineSegment(sketch, "E28.8.0.1", {"start": v(100.7, 0.25) * mm, "end": v(100.7, -0.25) * mm});
            skLineSegment(sketch, "E28.8.0.2", {"start": v(101.3, 0.25) * mm, "end": v(100.7, 0.25) * mm});
            skLineSegment(sketch, "E28.8.0.3", {"start": v(101.3, 0.25) * mm, "end": v(101.3, -0.25) * mm});
            skLineSegment(sketch, "E28.direction1", {"start": v(20.7, -0.25) * mm, "end": v(30.7, -0.25) * mm, "construction": true});
            skLineSegment(sketch, "E29", {"start": v(0, 0) * mm, "end": v(0, 10) * mm});
            skLineSegment(sketch, "E30", {"start": v(-3.26, 5) * mm, "end": v(-7.75, 5) * mm});
            skPoint(sketch, "E30.startSnap0", {"position": v(0, 5) * mm});
            skLineSegment(sketch, "E31.MirrorCS", {"start": v(20.7, 9.75) * mm, "end": v(20.7, 10.25) * mm});
            skLineSegment(sketch, "E32.MirrorCS", {"start": v(21.3, 10.25) * mm, "end": v(20.7, 10.25) * mm});
            skLineSegment(sketch, "E33.MirrorCS", {"start": v(21.3, 9.75) * mm, "end": v(20.7, 9.75) * mm});
            skLineSegment(sketch, "E34.MirrorCS", {"start": v(31.3, 9.75) * mm, "end": v(30.7, 9.75) * mm});
            skLineSegment(sketch, "E35.MirrorCS", {"start": v(30.7, 9.75) * mm, "end": v(30.7, 10.25) * mm});
            skLineSegment(sketch, "E36.MirrorCS", {"start": v(31.3, 9.75) * mm, "end": v(31.3, 10.25) * mm});
            skLineSegment(sketch, "E37.MirrorCS", {"start": v(31.3, 10.25) * mm, "end": v(30.7, 10.25) * mm});
            skLineSegment(sketch, "E38.MirrorCS", {"start": v(21.3, 9.75) * mm, "end": v(21.3, 10.25) * mm});
            skLineSegment(sketch, "E39.MirrorCS", {"start": v(101.3, 10.25) * mm, "end": v(100.7, 10.25) * mm});
            skLineSegment(sketch, "E40.MirrorCS", {"start": v(111.3, 9.75) * mm, "end": v(111.3, 10.25) * mm});
            skLineSegment(sketch, "E41.MirrorCS", {"start": v(80.7, 9.75) * mm, "end": v(80.7, 10.25) * mm});
            skLineSegment(sketch, "E42.MirrorCS", {"start": v(71.3, 9.75) * mm, "end": v(70.7, 9.75) * mm});
            skLineSegment(sketch, "E43.MirrorCS", {"start": v(51.3, 9.75) * mm, "end": v(50.7, 9.75) * mm});
            skLineSegment(sketch, "E44.MirrorCS", {"start": v(90.7, 9.75) * mm, "end": v(90.7, 10.25) * mm});
            skLineSegment(sketch, "E45.MirrorCS", {"start": v(91.3, 9.75) * mm, "end": v(91.3, 10.25) * mm});
            skLineSegment(sketch, "E46.MirrorCS", {"start": v(61.3, 9.75) * mm, "end": v(60.7, 9.75) * mm});
            skLineSegment(sketch, "E47.MirrorCS", {"start": v(91.3, 10.25) * mm, "end": v(90.7, 10.25) * mm});
            skLineSegment(sketch, "E48.MirrorCS", {"start": v(71.3, 10.25) * mm, "end": v(70.7, 10.25) * mm});
            skLineSegment(sketch, "E49.MirrorCS", {"start": v(41.3, 10.25) * mm, "end": v(40.7, 10.25) * mm});
            skLineSegment(sketch, "E50.MirrorCS", {"start": v(101.3, 9.75) * mm, "end": v(101.3, 10.25) * mm});
            skLineSegment(sketch, "E51.MirrorCS", {"start": v(51.3, 9.75) * mm, "end": v(51.3, 10.25) * mm});
            skLineSegment(sketch, "E52.MirrorCS", {"start": v(91.3, 9.75) * mm, "end": v(90.7, 9.75) * mm});
            skLineSegment(sketch, "E53.MirrorCS", {"start": v(111.3, 9.75) * mm, "end": v(110.7, 9.75) * mm});
            skLineSegment(sketch, "E54.MirrorCS", {"start": v(40.7, 9.75) * mm, "end": v(40.7, 10.25) * mm});
            skLineSegment(sketch, "E55.MirrorCS", {"start": v(41.3, 9.75) * mm, "end": v(41.3, 10.25) * mm});
            skLineSegment(sketch, "E56.MirrorCS", {"start": v(50.7, 9.75) * mm, "end": v(50.7, 10.25) * mm});
            skLineSegment(sketch, "E57.MirrorCS", {"start": v(70.7, 9.75) * mm, "end": v(70.7, 10.25) * mm});
            skLineSegment(sketch, "E58.MirrorCS", {"start": v(81.3, 9.75) * mm, "end": v(81.3, 10.25) * mm});
            skLineSegment(sketch, "E59.MirrorCS", {"start": v(71.3, 9.75) * mm, "end": v(71.3, 10.25) * mm});
            skLineSegment(sketch, "E60.MirrorCS", {"start": v(51.3, 10.25) * mm, "end": v(50.7, 10.25) * mm});
            skLineSegment(sketch, "E61.MirrorCS", {"start": v(81.3, 9.75) * mm, "end": v(80.7, 9.75) * mm});
            skLineSegment(sketch, "E62.MirrorCS", {"start": v(101.3, 9.75) * mm, "end": v(100.7, 9.75) * mm});
            skLineSegment(sketch, "E63.MirrorCS", {"start": v(41.3, 9.75) * mm, "end": v(40.7, 9.75) * mm});
            skLineSegment(sketch, "E64.MirrorCS", {"start": v(61.3, 9.75) * mm, "end": v(61.3, 10.25) * mm});
            skLineSegment(sketch, "E65.MirrorCS", {"start": v(61.3, 10.25) * mm, "end": v(60.7, 10.25) * mm});
            skLineSegment(sketch, "E66.MirrorCS", {"start": v(81.3, 10.25) * mm, "end": v(80.7, 10.25) * mm});
            skLineSegment(sketch, "E67.MirrorCS", {"start": v(111.3, 10.25) * mm, "end": v(110.7, 10.25) * mm});
            skLineSegment(sketch, "E68.MirrorCS", {"start": v(100.7, 9.75) * mm, "end": v(100.7, 10.25) * mm});
            skLineSegment(sketch, "E69.MirrorCS", {"start": v(60.7, 9.75) * mm, "end": v(60.7, 10.25) * mm});
            skLineSegment(sketch, "E70.MirrorCS", {"start": v(110.7, 9.75) * mm, "end": v(110.7, 10.25) * mm});
            skPoint(sketch, "E71.MirrorP", {"position": v(21, 10) * mm});
            skLineSegment(sketch, "E72.MirrorCS", {"start": v(20.7, 10.25) * mm, "end": v(30.7, 10.25) * mm, "construction": true});
            skSolve(sketch);
        }
        {
            var Q0;
            Q0=qSketchRegion(id+"F2",true);
            var Q1;
            Q1=sQuery(id+"F2.wireOp",EDGE,"E29");
            revolve(context, id + "F3", {"operationType" : NewBodyOperationType.REMOVE, "entities" : qUnion([Q0]), "axis" : qUnion([Q1]), "revolveType" : RevolveType.FULL, "oppositeDirection" : true});
        }
        {
            var Q0;
            {var subQ5=sQuery(id+"F0.wireOp",EDGE,"E25.top");Q0=makeQuery(id+"F0.imprint","IMPRINT",FACE,{"disambiguationData":[TD([[makeQuery(id+"F0.imprint","IMPRINT",EDGE,{"derivedFrom":subQ5}),-1.0]])]});}
            extrude(context, id + "F4", {"entities" : qUnion([Q0]), "depth" : 12 * mm, "offsetDistance" : 25 * mm, "hasSecondDirection" : true, "secondDirectionOppositeDirection" : true, "secondDirectionDepth" : 11 * mm});
        }
        {
            var Q0;
            Q0=makeQuery(id+"F4.opExtrude","CAP_FACE",FACE,{"disambiguationData":[OSD([sQuery(id+"F0.wireOp",EDGE,"E24"),sQuery(id+"F0.wireOp",EDGE,"E25.top"),sQuery(id+"F0.wireOp",EDGE,"E25.left"),sQuery(id+"F0.wireOp",EDGE,"E25.right")])],"isStart":true});
            var sketch = newSketch(context, id + "F5", { "sketchPlane" : qUnion([Q0])});
            skCircle(sketch, "E73", {"center": v(0, 0) * mm, "radius": 5 * mm});
            skLineSegment(sketch, "E74.bottom", {"start": v(5, 0) * mm, "end": v(-5, 0) * mm});
            skLineSegment(sketch, "E74.top", {"start": v(5, -110) * mm, "end": v(-5, -110) * mm});
            skLineSegment(sketch, "E74.left", {"start": v(5, 0) * mm, "end": v(5, -110) * mm});
            skLineSegment(sketch, "E74.right", {"start": v(-5, 0) * mm, "end": v(-5, -110) * mm});
            skPoint(sketch, "E74.middle", {"position": v(0, -55) * mm});
            skLineSegment(sketch, "E75", {"start": v(0, -100) * mm, "end": v(0, -18.14) * mm, "construction": true});
            skPoint(sketch, "E75.startSnap0", {"position": v(0, -110) * mm});
            skPoint(sketch, "E75.endSnap0", {"position": v(0, -5) * mm});
            skArc(sketch, "E76.0.startCap", {"start": v(2, -100) * mm, "mid": v(0, -102) * mm, "end": v(-2, -100) * mm});
            skArc(sketch, "E76.0.endCap", {"start": v(-2, -18.14) * mm, "mid": v(0, -16.14) * mm, "end": v(2, -18.14) * mm});
            skLineSegment(sketch, "E76.0.left", {"start": v(-2, -100) * mm, "end": v(-2, -18.14) * mm});
            skLineSegment(sketch, "E76.0.right", {"start": v(2, -100) * mm, "end": v(2, -18.14) * mm});
            skSolve(sketch);
        }
        {
            var Q0;
            Q0 = qSketchRegion(id + "F5", true);
            extrude(context, id + "F6", {"entities" : qUnion([Q0]), "operationType" : NewBodyOperationType.ADD, "oppositeDirection" : true, "depth" : 10 * mm, "offsetDistance" : 25 * mm});
        }
        {
            var Q0;
            Q0=makeQuery(id+"F6.opExtrude","CAP_EDGE",EDGE,{"disambiguationData":[OSD([sQuery(id+"F5.wireOp",EDGE,"E74.right")])],"isStart":true});
            var Q1;
            Q1=makeQuery(id+"F6.opExtrude","SWEPT_FACE",FACE,{"disambiguationData":[OSD([sQuery(id+"F5.wireOp",EDGE,"E74.right")])]});
            var Q2;
            Q2=makeQuery(id+"F6.opExtrude","SWEPT_FACE",FACE,{"disambiguationData":[OSD([sQuery(id+"F5.wireOp",EDGE,"E74.left")])]});
            var Q3;
            Q3=makeQuery(id+"F6.opExtrude","SWEPT_FACE",FACE,{"disambiguationData":[OSD([sQuery(id+"F5.wireOp",EDGE,"E74.top")])]});
            fillet(context, id + "F7", {"entities" : qUnion([Q0, Q1, Q2, Q3]), "radius" : 2 * mm, "tangentPropagation" : true, "allowEdgeOverflow" : false});
        }
        {
            var Q0;
            Q0=makeQuery(id+"F6.boolean.opBoolean","MERGE",FACE,{"derivedFrom":[makeQuery(id+"F4.opExtrude","CAP_FACE",FACE,{"disambiguationData":[OSD([sQuery(id+"F0.wireOp",EDGE,"E24"),sQuery(id+"F0.wireOp",EDGE,"E25.top"),sQuery(id+"F0.wireOp",EDGE,"E25.left"),sQuery(id+"F0.wireOp",EDGE,"E25.right")])],"isStart":true}),makeQuery(id+"F6.opExtrude","CAP_FACE",FACE,{"disambiguationData":[OSD([sQuery(id+"F5.wireOp",EDGE,"E73"),sQuery(id+"F5.wireOp",EDGE,"E74.top"),sQuery(id+"F5.wireOp",EDGE,"E74.left"),sQuery(id+"F5.wireOp",EDGE,"E74.right"),sQuery(id+"F5.wireOp",EDGE,"E76.0.startCap"),sQuery(id+"F5.wireOp",EDGE,"E76.0.endCap"),sQuery(id+"F5.wireOp",EDGE,"E76.0.left"),sQuery(id+"F5.wireOp",EDGE,"E76.0.right")])],"isStart":true})]});
            var sketch = newSketch(context, id + "F8", { "sketchPlane" : qUnion([Q0])});
            skCircle(sketch, "E77", {"center": v(0, -104.9) * mm, "radius": 2 * mm});
            skPoint(sketch, "E77.centerSnap0", {"position": v(0, -108) * mm});
            skSolve(sketch);
        }
        {
            var Q0;
            Q0 = qSketchRegion(id + "F8", true);
            extrude(context, id + "F9", {"entities" : qUnion([Q0]), "operationType" : NewBodyOperationType.ADD, "depth" : 10 * mm, "offsetDistance" : 25 * mm, "hasDraft" : true, "draftAngle" : 12 * degree});
        }
        {
            var Q0;
            Q0=makeQuery(id+"F9.opExtrude","CAP_EDGE",EDGE,{"disambiguationData":[OSD([sQuery(id+"F8.wireOp",EDGE,"E77")])],"isStart":false});
            var Q1;
            Q1=makeQuery(id+"F9.opExtrude","CAP_EDGE",EDGE,{"disambiguationData":[OSD([sQuery(id+"F8.wireOp",EDGE,"E77")])],"isStart":true});
            fillet(context, id + "F10", {"entities" : qUnion([Q0, Q1]), "radius" : 2 * mm, "tangentPropagation" : true, "allowEdgeOverflow" : false});
        }
        {
            var Q0;
            Q0=makeQuery(id+"F1.opExtrude","CAP_EDGE",EDGE,{"disambiguationData":[OSD([sQuery(id+"F0.wireOp",EDGE,"E0")])],"isStart":true});
            var Q1;
            Q1=makeQuery(id+"F1.opExtrude","CAP_EDGE",EDGE,{"disambiguationData":[OSD([sQuery(id+"F0.wireOp",EDGE,"E0")])],"isStart":false});
            fillet(context, id + "F11", {"entities" : qUnion([Q0, Q1]), "radius" : 1 * mm, "tangentPropagation" : true, "allowEdgeOverflow" : false});
        }
        {
            var Q0;
            Q0=makeQuery(id+"F4.opExtrude","SWEPT_BODY",BODY,{"disambiguationData":[OSD([sQuery(id+"F0.wireOp",EDGE,"E24"),sQuery(id+"F0.wireOp",EDGE,"E25.top"),sQuery(id+"F0.wireOp",EDGE,"E25.left"),sQuery(id+"F0.wireOp",EDGE,"E25.right")])]});
            deleteBodies(context, id + "F12", {"entities" : qUnion([Q0])});
        }
    });
